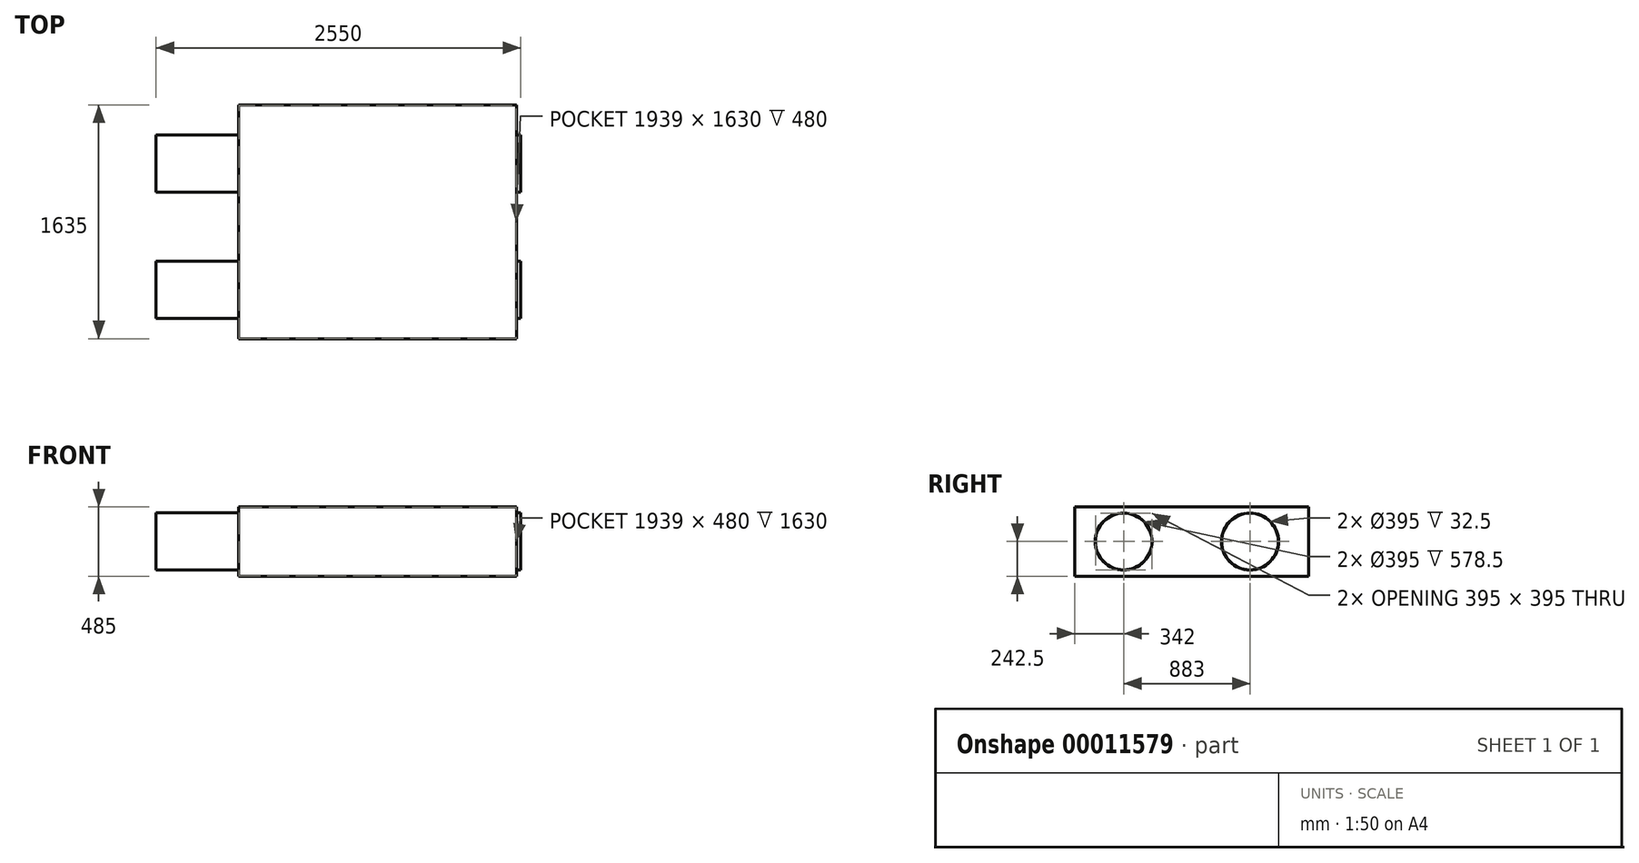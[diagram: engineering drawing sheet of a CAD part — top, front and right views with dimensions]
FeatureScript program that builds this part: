
annotation { "Feature Type Name" : "Feature", "Feature Type Description" : "" }
export const myFeature = defineFeature(function(context is Context, id is Id, definition is map)
    precondition{}
    {
        {
            var Q0;
            Q0=qCreatedBy(makeId("Top.planeOp"),FACE);
            var sketch = newSketch(context, id + "F0", { "sketchPlane" : qUnion([Q0])});
            skLineSegment(sketch, "E0.rect.bottom", {"start": v(-972, 817.5) * mm, "end": v(972, 817.5) * mm});
            skLineSegment(sketch, "E0.rect.top", {"start": v(-972, -817.5) * mm, "end": v(972, -817.5) * mm});
            skLineSegment(sketch, "E0.rect.left", {"start": v(-972, 817.5) * mm, "end": v(-972, -817.5) * mm});
            skLineSegment(sketch, "E0.rect.right", {"start": v(972, 817.5) * mm, "end": v(972, -817.5) * mm});
            skPoint(sketch, "E0.rect.middle", {"position": v(0, 0) * mm});
            skSolve(sketch);
        }
        {
            var Q0;
            Q0=makeQuery(id+"F0.imprint","IMPRINT",FACE,{"disambiguationData":[TD([[makeQuery(id+"F0.imprint","IMPRINT",EDGE,{"derivedFrom":sQuery(id+"F0.wireOp",EDGE,"E0.rect.bottom")}),-1.0]])]});
            extrude(context, id + "F1", {"entities" : qUnion([Q0]), "depth" : 485 * mm});
        }
        {
            var Q0;
            Q0=makeQuery(id+"F1.opExtrude","SWEPT_FACE",FACE,{"disambiguationData":[OSD([sQuery(id+"F0.wireOp",EDGE,"E0.rect.left")])]});
            var sketch = newSketch(context, id + "F2", { "sketchPlane" : qUnion([Q0])});
            skCircle(sketch, "E1", {"center": v(-407.5, 242.5) * mm, "radius": 200 * mm});
            skCircle(sketch, "E2", {"center": v(475.5, 242.5) * mm, "radius": 200 * mm});
            skSolve(sketch);
        }
        {
            var Q0;
            Q0 = qSketchRegion(id + "F2", true);
            extrude(context, id + "F3", {"entities" : qUnion([Q0]), "operationType" : NewBodyOperationType.ADD, "depth" : 30 * mm, "hasSecondDirection" : true, "secondDirectionOppositeDirection" : true, "secondDirectionDepth" : 1974 * mm});
        }
        {
            var Q0;
            Q0=makeQuery(id+"F3.opExtrude","CAP_FACE",FACE,{"disambiguationData":[OSD([sQuery(id+"F2.wireOp",EDGE,"E2")])],"isStart":true});
            var Q1;
            Q1=makeQuery(id+"F3.opExtrude","CAP_FACE",FACE,{"disambiguationData":[OSD([sQuery(id+"F2.wireOp",EDGE,"E1")])],"isStart":true});
            var Q2;
            Q2=makeQuery(id+"F3.opExtrude","CAP_FACE",FACE,{"disambiguationData":[OSD([sQuery(id+"F2.wireOp",EDGE,"E1")])],"isStart":false});
            var Q3;
            Q3=makeQuery(id+"F3.opExtrude","CAP_FACE",FACE,{"disambiguationData":[OSD([sQuery(id+"F2.wireOp",EDGE,"E2")])],"isStart":false});
            shell(context, id + "F4", {"entities" : qUnion([Q0, Q1, Q2, Q3]), "thickness" : 2.5 * mm});
        }
        {
            var Q0;
            Q0=makeQuery(id+"F3.opExtrude","CAP_FACE",FACE,{"disambiguationData":[OSD([sQuery(id+"F2.wireOp",EDGE,"E1")])],"isStart":false});
            extrude(context, id + "F5", {"entities" : qUnion([Q0]), "operationType" : NewBodyOperationType.ADD, "depth" : 546 * mm});
        }
        {
            var Q0;
            Q0=makeQuery(id+"F3.opExtrude","CAP_FACE",FACE,{"disambiguationData":[OSD([sQuery(id+"F2.wireOp",EDGE,"E2")])],"isStart":false});
            extrude(context, id + "F6", {"entities" : qUnion([Q0]), "operationType" : NewBodyOperationType.ADD, "depth" : 546 * mm});
        }
    });
